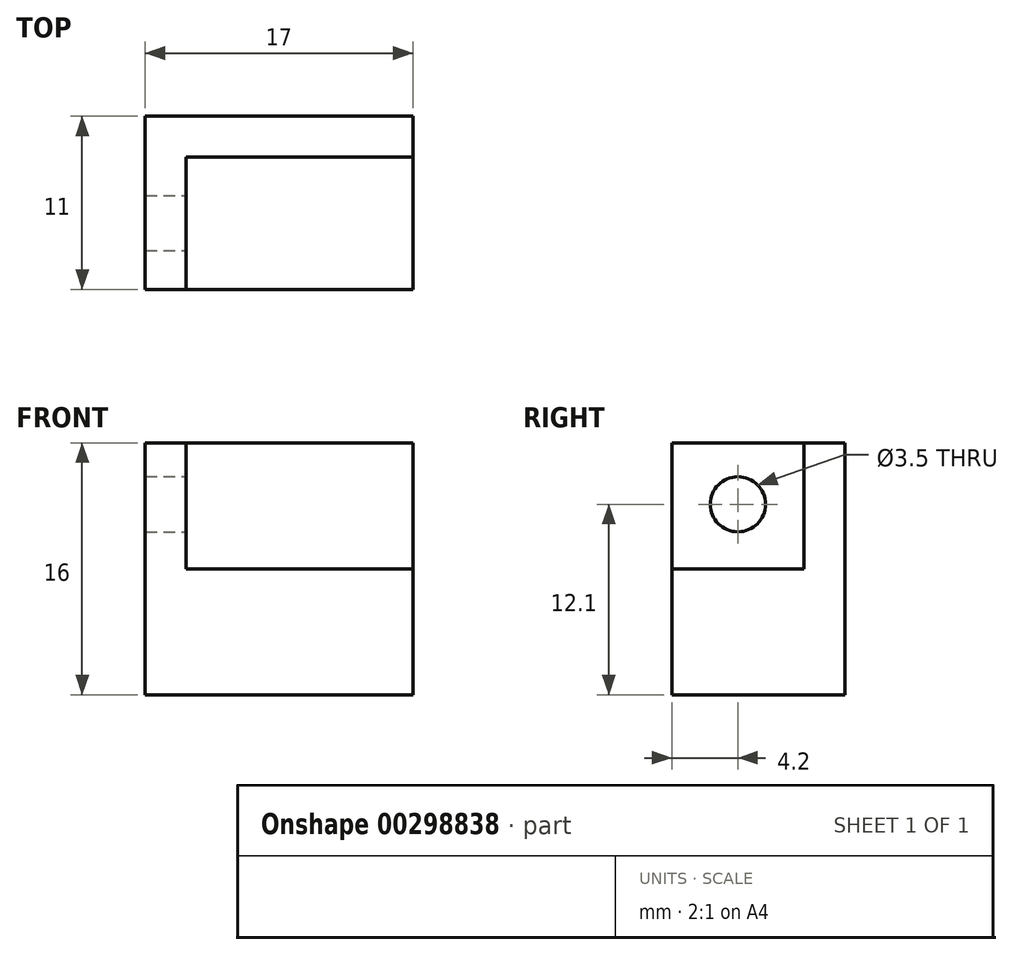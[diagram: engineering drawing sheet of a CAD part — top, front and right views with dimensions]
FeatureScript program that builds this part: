
annotation { "Feature Type Name" : "Feature", "Feature Type Description" : "" }
export const myFeature = defineFeature(function(context is Context, id is Id, definition is map)
    precondition{}
    {
        {
            var Q0;
            Q0=qCreatedBy(makeId("Front.planeOp"),FACE);
            var sketch = newSketch(context, id + "F0", { "sketchPlane" : qUnion([Q0])});
            skLineSegment(sketch, "E0", {"start": v(0, 0) * mm, "end": v(0, 8) * mm});
            skLineSegment(sketch, "E1", {"start": v(0, 8) * mm, "end": v(17, 8) * mm});
            skLineSegment(sketch, "E2", {"start": v(17, 8) * mm, "end": v(17, 0) * mm});
            skLineSegment(sketch, "E3", {"start": v(17, 0) * mm, "end": v(0, 0) * mm});
            skSolve(sketch);
        }
        {
            var Q0;
            Q0=makeQuery(id+"F0.imprint","IMPRINT",FACE,{"disambiguationData":[TD([[makeQuery(id+"F0.imprint","IMPRINT",EDGE,{"derivedFrom":sQuery(id+"F0.wireOp",EDGE,"E0")}),-1.0]])]});
            extrude(context, id + "F1", {"entities" : qUnion([Q0]), "depth" : 11 * mm});
        }
        {
            var Q0;
            Q0=makeQuery(id+"F1.opExtrude","SWEPT_FACE",FACE,{"disambiguationData":[OSD([sQuery(id+"F0.wireOp",EDGE,"E1")])]});
            var sketch = newSketch(context, id + "F2", { "sketchPlane" : qUnion([Q0])});
            skPoint(sketch, "E4", {"position": v(2.6, -7.94) * mm});
            skPoint(sketch, "E5", {"position": v(2.6, -2.6) * mm});
            skLineSegment(sketch, "E6", {"start": v(2.6, -11) * mm, "end": v(2.6, -2.6) * mm});
            skLineSegment(sketch, "E7", {"start": v(17, -2.6) * mm, "end": v(2.6, -2.6) * mm});
            skSolve(sketch);
        }
        {
            var Q0;
            {var subQ4=sQuery(id+"F2.wireOp",EDGE,"E6");Q0=makeQuery(id+"F2.imprint","IMPRINT",FACE,{"disambiguationData":[TD([[makeQuery(id+"F2.imprint","IMPRINT",EDGE,{"derivedFrom":subQ4}),1.0]])]});}
            extrude(context, id + "F3", {"entities" : qUnion([Q0]), "operationType" : NewBodyOperationType.ADD, "depth" : 8 * mm});
        }
        {
            var Q0;
            Q0=makeQuery(id+"F3.opExtrude","SWEPT_FACE",FACE,{"disambiguationData":[OSD([sQuery(id+"F2.wireOp",EDGE,"E6")])]});
            var sketch = newSketch(context, id + "F4", { "sketchPlane" : qUnion([Q0])});
            skPoint(sketch, "E8", {"position": v(-6.8, 12.1) * mm});
            skPoint(sketch, "E9", {"position": v(-6.8, 14.7) * mm});
            skPoint(sketch, "E10", {"position": v(-6.8, 13.4) * mm});
            skSolve(sketch);
        }
        {
            var Q0;
            Q0=sQuery(id+"F4.wireOp",VERTEX,"E8");
            var Q1;
            Q1=makeQuery(id+"F1.opExtrude","SWEPT_BODY",BODY,{"disambiguationData":[OSD([sQuery(id+"F0.wireOp",EDGE,"E0"),sQuery(id+"F0.wireOp",EDGE,"E1"),sQuery(id+"F0.wireOp",EDGE,"E2"),sQuery(id+"F0.wireOp",EDGE,"E3")])]});
            hole(context, id + "F5", {"style" : HoleStyle.SIMPLE, "endStyle" : HoleEndStyle.THROUGH, "holeDiameter" : 3.5 * mm, "tappedDepth" : 12 * mm, "tapClearance" : 3, "locations" : qUnion([Q0]), "scope" : qUnion([Q1])});
        }
    });
